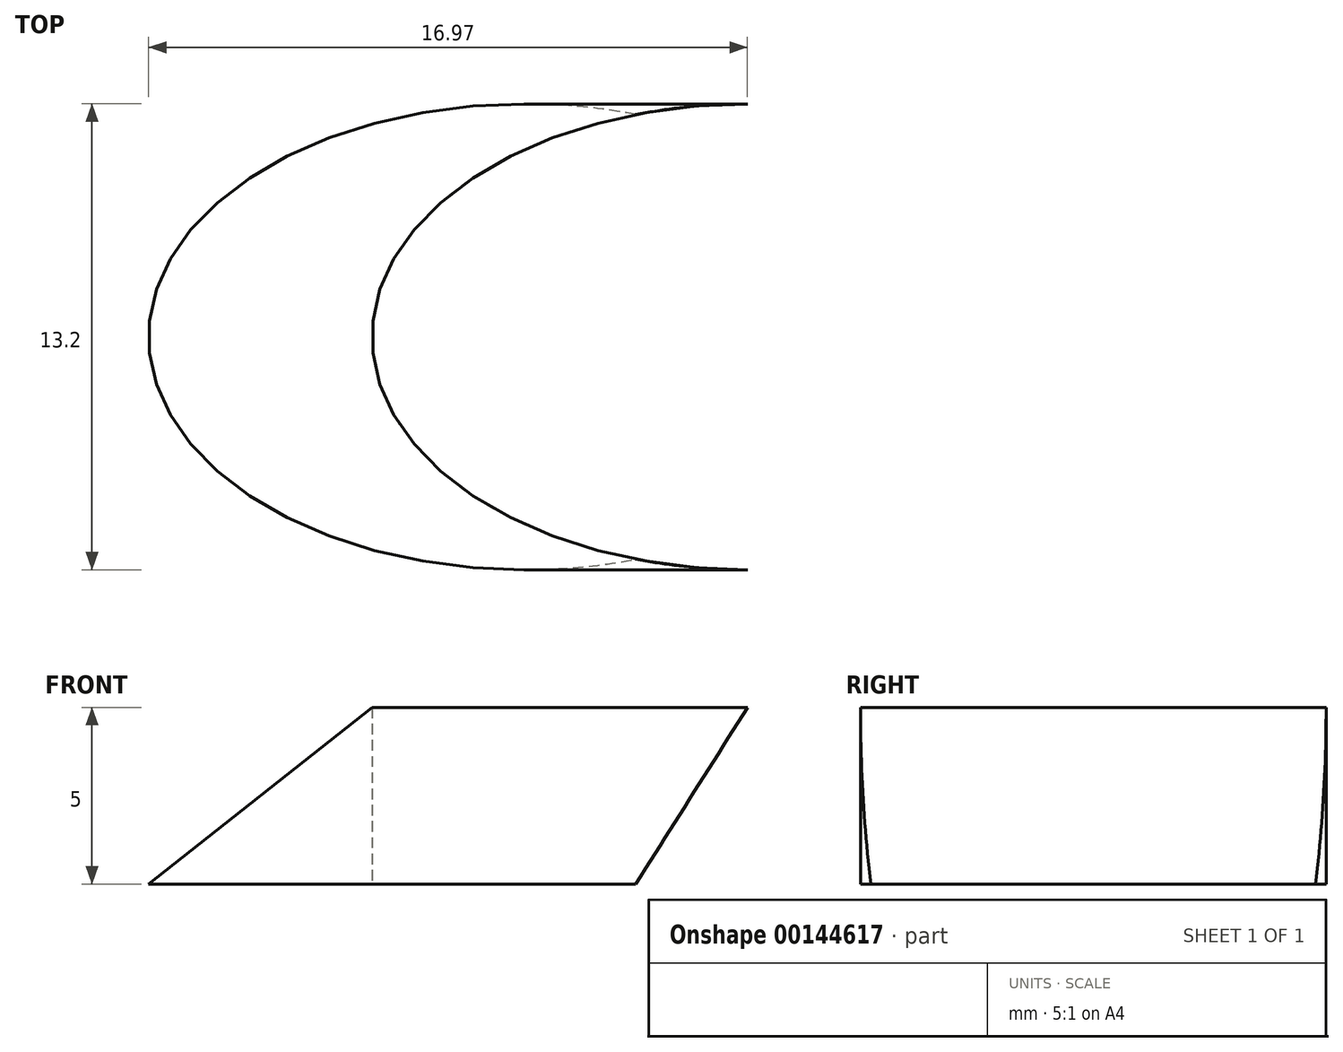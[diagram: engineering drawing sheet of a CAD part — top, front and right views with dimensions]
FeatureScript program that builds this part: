
annotation { "Feature Type Name" : "Feature", "Feature Type Description" : "" }
export const myFeature = defineFeature(function(context is Context, id is Id, definition is map)
    precondition{}
    {
        {
            var Q0;
            Q0=qCreatedBy(makeId("Top.planeOp"),FACE);
            var sketch = newSketch(context, id + "F0", { "sketchPlane" : qUnion([Q0])});
            skLineSegment(sketch, "E0.bottom", {"start": v(-142.12, 60.55) * mm, "end": v(119.55, 60.55) * mm});
            skLineSegment(sketch, "E0.top", {"start": v(-142.12, -82.82) * mm, "end": v(119.55, -82.82) * mm});
            skLineSegment(sketch, "E0.left", {"start": v(-142.12, 60.55) * mm, "end": v(-142.12, -82.82) * mm});
            skLineSegment(sketch, "E0.right", {"start": v(119.55, 60.55) * mm, "end": v(119.55, -82.82) * mm});
            skSolve(sketch);
        }
        {
            var Q0;
            Q0=makeQuery(id+"F0.imprint","IMPRINT",FACE,{"disambiguationData":[TD([[makeQuery(id+"F0.imprint","IMPRINT",EDGE,{"derivedFrom":sQuery(id+"F0.wireOp",EDGE,"E0.bottom")}),-1.0]])]});
            extrude(context, id + "F1", {"entities" : qUnion([Q0]), "depth" : 5 * mm});
        }
        {
            var Q0;
            Q0=makeQuery(id+"F1.opExtrude","CAP_FACE",FACE,{"disambiguationData":[OSD([sQuery(id+"F0.wireOp",EDGE,"E0.bottom"),sQuery(id+"F0.wireOp",EDGE,"E0.top"),sQuery(id+"F0.wireOp",EDGE,"E0.left"),sQuery(id+"F0.wireOp",EDGE,"E0.right")])],"isStart":false});
            var sketch = newSketch(context, id + "F2", { "sketchPlane" : qUnion([Q0])});
            skCircle(sketch, "E1", {"center": v(-101.05, -26.73) * mm, "radius": 19.41 * mm});
            skSolve(sketch);
        }
        {
            var Q0;
            Q0=makeQuery(id+"F2.imprint","IMPRINT",FACE,{"disambiguationData":[TD([[makeQuery(id+"F2.imprint","IMPRINT",EDGE,{"derivedFrom":sQuery(id+"F2.wireOp",EDGE,"E1")}),1.0]])]});
            extrude(context, id + "F3", {"entities" : qUnion([Q0]), "operationType" : NewBodyOperationType.REMOVE, "oppositeDirection" : true, "depth" : 2 * mm});
        }
        {
            var Q0;
            Q0=qCreatedBy(makeId("Front.planeOp"),FACE);
            var sketch = newSketch(context, id + "F4", { "sketchPlane" : qUnion([Q0])});
            skLineSegment(sketch, "E2", {"start": v(-36.9, -23.3) * mm, "end": v(38.46, 36.24) * mm});
            skSolve(sketch);
        }
        {
            var Q0;
            Q0=sQuery(id+"F4.wireOp",VERTEX,"E2.end");
            var Q1;
            Q1=sQuery(id+"F4.wireOp",EDGE,"E2");
            cPlane(context, id + "F5", {"entities" : qUnion([Q0, Q1]), "cplaneType" : CPlaneType.LINE_POINT, "offset" : 25.4 * mm, "width" : 152.4 * mm, "height" : 152.4 * mm});
        }
        {
            var Q0;
            Q0=qCreatedBy(id+"F5.planeOp",FACE);
            var sketch = newSketch(context, id + "F6", { "sketchPlane" : qUnion([Q0])});
            skPoint(sketch, "E3.0", {"position": v(0, 4.6) * mm});
            skCircle(sketch, "E4", {"center": v(0, 4.6) * mm, "radius": 6.6 * mm});
            skSolve(sketch);
        }
        {
            var Q0;
            Q0=makeQuery(id+"F6.imprint","IMPRINT",FACE,{"disambiguationData":[TD([[makeQuery(id+"F6.imprint","IMPRINT",EDGE,{"derivedFrom":sQuery(id+"F6.wireOp",EDGE,"E4")}),1.0]])]});
            var Q1;
            Q1=sQuery(id+"F4.wireOp",VERTEX,"E2.start");
            extrude(context, id + "F7", {"entities" : qUnion([Q0]), "endBound" : BoundingType.UP_TO_VERTEX, "oppositeDirection" : true, "endBoundEntityVertex" : qUnion([Q1]), "depth" : 25.4 * mm});
        }
        {
            var Q0;
            Q0=makeQuery(id+"F7.opExtrude","SWEPT_BODY",BODY,{"disambiguationData":[OSD([sQuery(id+"F6.wireOp",EDGE,"E4")])]});
            var Q1;
            Q1=makeQuery(id+"F1.opExtrude","SWEPT_BODY",BODY,{"disambiguationData":[OSD([sQuery(id+"F0.wireOp",EDGE,"E0.bottom"),sQuery(id+"F0.wireOp",EDGE,"E0.top"),sQuery(id+"F0.wireOp",EDGE,"E0.left"),sQuery(id+"F0.wireOp",EDGE,"E0.right")])]});
            booleanBodies(context, id + "F8", {"operationType" : BooleanOperationType.SUBTRACTION, "tools" : qUnion([Q0]), "targets" : qUnion([Q1])});
        }
        {
            var Q0;
            Q0=makeQuery(id+"F1.opExtrude","CAP_FACE",FACE,{"disambiguationData":[OSD([sQuery(id+"F0.wireOp",EDGE,"E0.bottom"),sQuery(id+"F0.wireOp",EDGE,"E0.top"),sQuery(id+"F0.wireOp",EDGE,"E0.left"),sQuery(id+"F0.wireOp",EDGE,"E0.right")])],"isStart":false});
            var Q1;
            Q1=makeQuery(id+"F1.opExtrude","CAP_VERTEX",VERTEX,{"disambiguationData":[OSD([sQuery(id+"F0.wireOp",EDGE,"E0.top"),sQuery(id+"F0.wireOp",EDGE,"E0.right")])],"isStart":true});
            extrude(context, id + "F9", {"entities" : qUnion([Q0]), "endBound" : BoundingType.UP_TO_VERTEX, "oppositeDirection" : true, "endBoundEntityVertex" : qUnion([Q1]), "depth" : 25.4 * mm});
        }
        {
            var Q0;
            Q0=makeQuery(id+"F1.opExtrude","SWEPT_BODY",BODY,{"disambiguationData":[OSD([sQuery(id+"F0.wireOp",EDGE,"E0.bottom"),sQuery(id+"F0.wireOp",EDGE,"E0.top"),sQuery(id+"F0.wireOp",EDGE,"E0.left"),sQuery(id+"F0.wireOp",EDGE,"E0.right")])]});
            var Q1;
            Q1=makeQuery(id+"F9.opExtrude","SWEPT_BODY",BODY,{"disambiguationData":[OSD([sQuery(id+"F0.wireOp",EDGE,"E0.bottom"),sQuery(id+"F0.wireOp",EDGE,"E0.top"),sQuery(id+"F0.wireOp",EDGE,"E0.left"),sQuery(id+"F0.wireOp",EDGE,"E0.right")])]});
            booleanBodies(context, id + "F10", {"operationType" : BooleanOperationType.SUBTRACTION, "tools" : qUnion([Q0]), "targets" : qUnion([Q1])});
        }
    });
